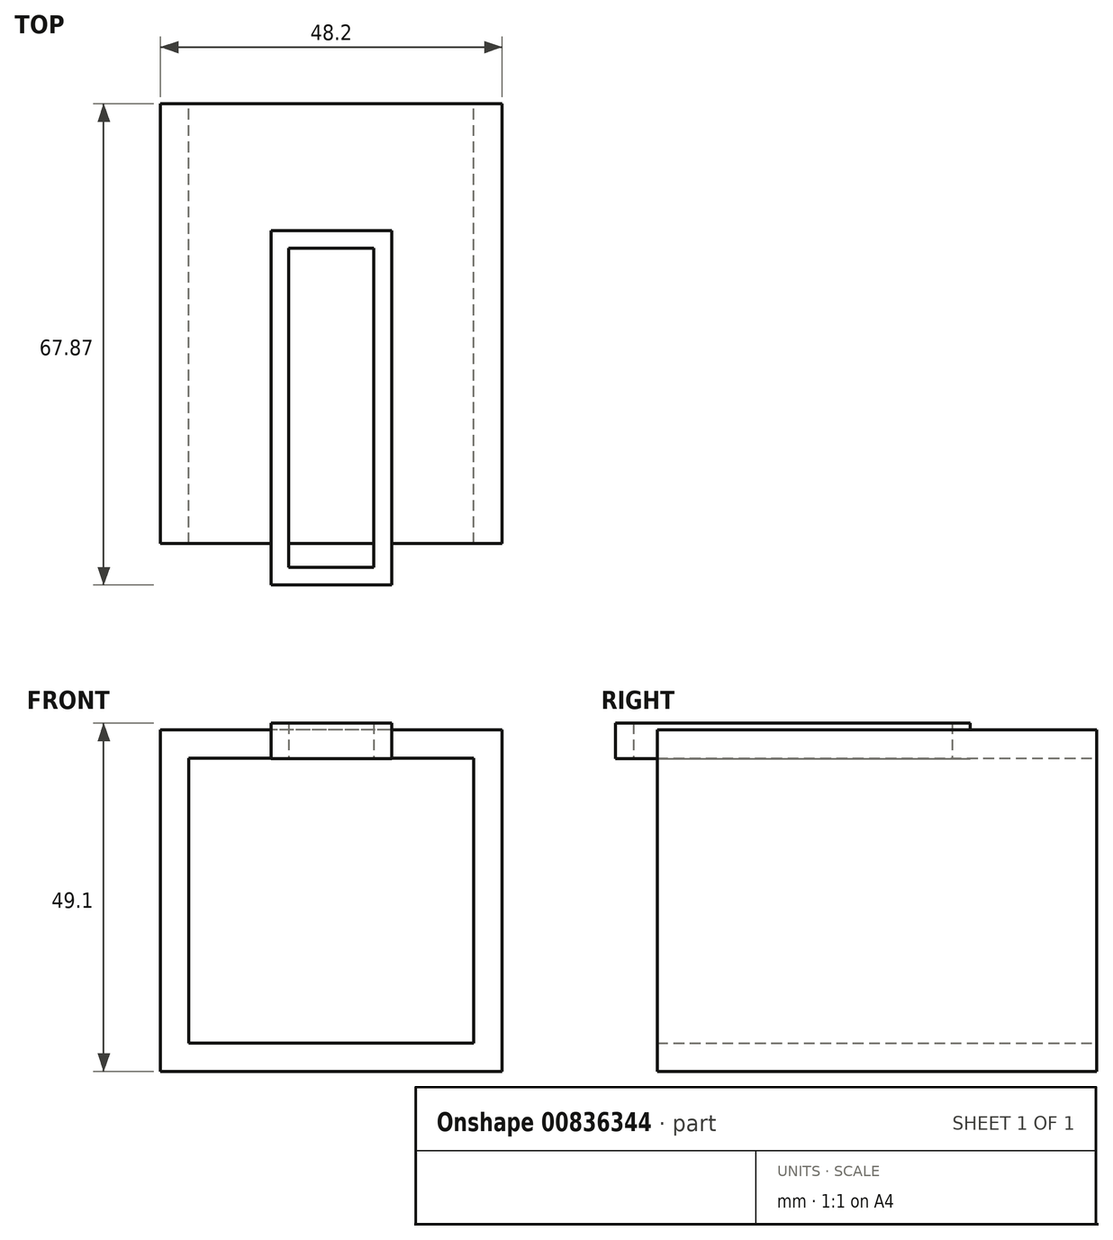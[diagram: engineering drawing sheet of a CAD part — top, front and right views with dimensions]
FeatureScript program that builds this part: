
annotation { "Feature Type Name" : "Feature", "Feature Type Description" : "" }
export const myFeature = defineFeature(function(context is Context, id is Id, definition is map)
    precondition{}
    {
        {
            var Q0;
            Q0=qCreatedBy(makeId("Front.planeOp"),FACE);
            var sketch = newSketch(context, id + "F0", { "sketchPlane" : qUnion([Q0])});
            skLineSegment(sketch, "E0.bottom", {"start": v(20.1, -20.1) * mm, "end": v(-20.1, -20.1) * mm});
            skLineSegment(sketch, "E0.top", {"start": v(20.1, 20.1) * mm, "end": v(-20.1, 20.1) * mm});
            skLineSegment(sketch, "E0.left", {"start": v(20.1, -20.1) * mm, "end": v(20.1, 20.1) * mm});
            skLineSegment(sketch, "E0.right", {"start": v(-20.1, -20.1) * mm, "end": v(-20.1, 20.1) * mm});
            skPoint(sketch, "E0.middle", {"position": v(0, 0) * mm});
            skLineSegment(sketch, "E1.0", {"start": v(24.1, 24.1) * mm, "end": v(-24.1, 24.1) * mm});
            skLineSegment(sketch, "E1.1", {"start": v(24.1, -24.1) * mm, "end": v(24.1, 24.1) * mm});
            skLineSegment(sketch, "E1.2", {"start": v(24.1, -24.1) * mm, "end": v(-24.1, -24.1) * mm});
            skLineSegment(sketch, "E1.3", {"start": v(-24.1, -24.1) * mm, "end": v(-24.1, 24.1) * mm});
            skSolve(sketch);
        }
        {
            var Q0;
            Q0 = qSketchRegion(id + "F0", true);
            extrude(context, id + "F1", {"entities" : qUnion([Q0]), "depth" : 62 * mm, "offsetDistance" : 25 * mm});
        }
        {
            var Q0;
            Q0=qCreatedBy(makeId("Top.planeOp"),FACE);
            var sketch = newSketch(context, id + "F2", { "sketchPlane" : qUnion([Q0])});
            skLineSegment(sketch, "E2.bottom", {"start": v(8.5, -67.87) * mm, "end": v(-8.5, -67.87) * mm});
            skLineSegment(sketch, "E2.top", {"start": v(8.5, -17.87) * mm, "end": v(-8.5, -17.87) * mm});
            skLineSegment(sketch, "E2.left", {"start": v(8.5, -67.87) * mm, "end": v(8.5, -17.87) * mm});
            skLineSegment(sketch, "E2.right", {"start": v(-8.5, -67.87) * mm, "end": v(-8.5, -17.87) * mm});
            skPoint(sketch, "E2.middle", {"position": v(0, -42.87) * mm});
            skSolve(sketch);
        }
        {
            var Q0;
            Q0 = qSketchRegion(id + "F2", true);
            extrude(context, id + "F3", {"entities" : qUnion([Q0]), "operationType" : NewBodyOperationType.ADD, "depth" : 25 * mm, "offsetDistance" : 25 * mm, "hasSecondDirection" : true, "secondDirectionOppositeDirection" : false, "secondDirectionDepth" : 20 * mm});
        }
        {
            var Q0;
            Q0=makeQuery(id+"F3.opExtrude","CAP_FACE",FACE,{"disambiguationData":[OSD([sQuery(id+"F2.wireOp",EDGE,"E2.bottom"),sQuery(id+"F2.wireOp",EDGE,"E2.top"),sQuery(id+"F2.wireOp",EDGE,"E2.left"),sQuery(id+"F2.wireOp",EDGE,"E2.right")])],"isStart":false});
            var Q1;
            Q1=makeQuery(id+"F3.opExtrude","CAP_FACE",FACE,{"disambiguationData":[OSD([sQuery(id+"F2.wireOp",EDGE,"E2.bottom"),sQuery(id+"F2.wireOp",EDGE,"E2.top"),sQuery(id+"F2.wireOp",EDGE,"E2.left"),sQuery(id+"F2.wireOp",EDGE,"E2.right")])],"isStart":true});
            shell(context, id + "F4", {"entities" : qUnion([Q0, Q1]), "thickness" : 2.5 * mm});
        }
    });
